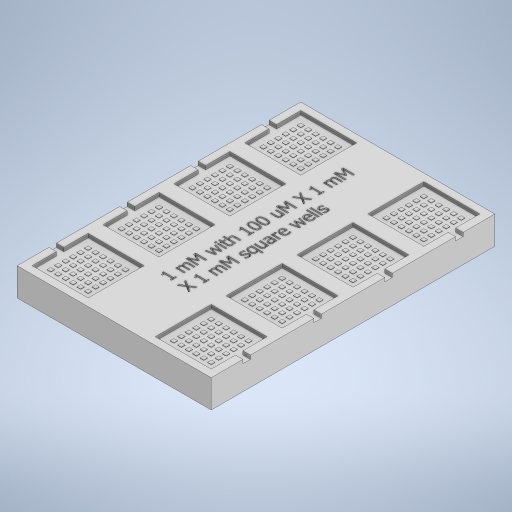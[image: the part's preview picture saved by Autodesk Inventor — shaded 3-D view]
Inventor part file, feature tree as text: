
AUTODESK INVENTOR PART (.ipt)
format: ipt  version: 2024 (Build 280153000, 153)  size: 4,618,752 bytes
history: native  units: in
note: dims shown in document units (in); Inventor stores cm internally (conversion verified against a paired STEP export)
features: extrude x4, sketch x3
ambient origin geometry x8: Origin, YZ Plane, XZ Plane, XY Plane, X Axis, Y Axis, Z Axis, Center Point
bodies: Solid1 (feature_tree)
feature tree (7):
  extrude  "Extrusion1"  Depth=2.0472in
  extrude  "Extrusion2"  Depth=0.5906in
  sketch  "Sketch3"  dims[d2=0.2953in d3=0.0in d4=0.5906in]
  sketch  "Sketch4"  dims[d10=0.0787in d11=0.0787in d12=0.0787in d13=0.0787in d15=0.8268in d16=0.8268in d17=0.0394in d18=0.0in d19=0.0787in d20=0.2559in d21=0.0787in d22=0.0787in d23=0.0787in d24=0.0787in d25=0.0787in d26=0.0787in d27=0.2559in d28=0.2559in d29=0.2559in d30=0.2559in d31=0.2559in d32=0.2559in d33=0.2559in d34=0.0787in d35=0.0394in d36=0.0787in d37=0.0787in d38=0.0394in d39=2.3622in d41=0.0787in d42=2.3622in d44=0.0787in d47=1.5748in d49=0.748in d50=0.7874in d52=1.2992in d55=0.0394in d56=0.0in d57=0.0039in d58=0.0in]
  extrude  "Extrusion3"  Depth=0.0787in
  extrude  "Extrusion4"  Depth=0.0787in
  sketch  "Sketch2"  dims[d0=2.9921in d1=2.0472in]
